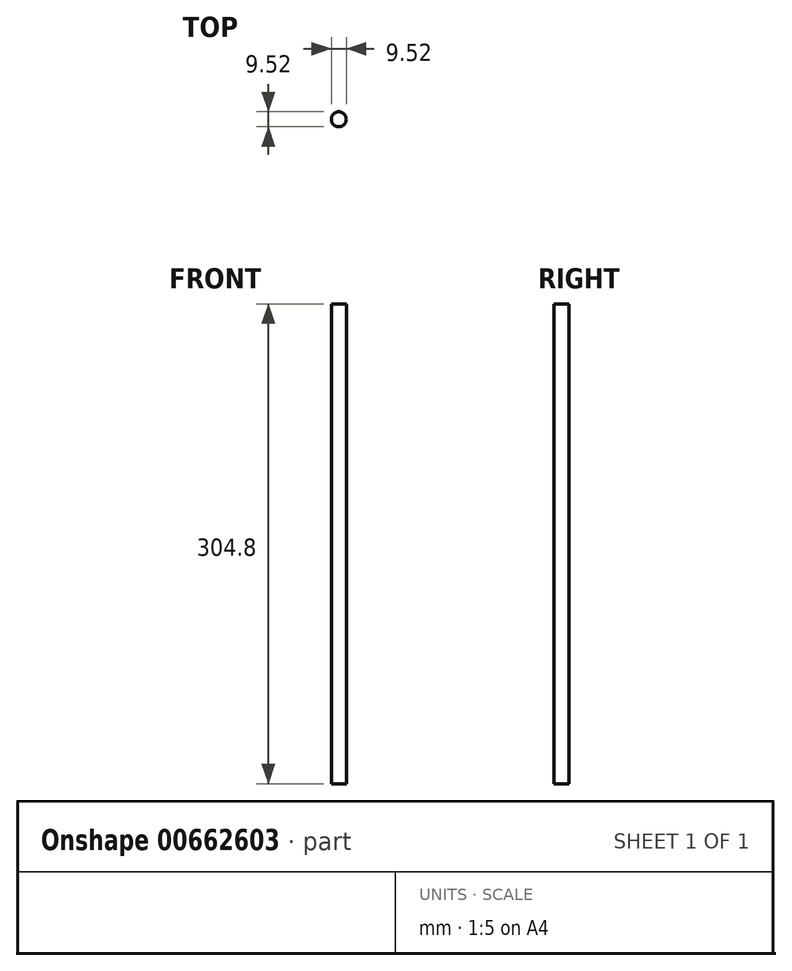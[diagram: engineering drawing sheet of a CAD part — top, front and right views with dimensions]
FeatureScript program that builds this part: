
annotation { "Feature Type Name" : "Feature", "Feature Type Description" : "" }
export const myFeature = defineFeature(function(context is Context, id is Id, definition is map)
    precondition{}
    {
        {
            var Q0;
            Q0=qCreatedBy(makeId("Top.planeOp"),FACE);
            var sketch = newSketch(context, id + "F0", { "sketchPlane" : qUnion([Q0])});
            skCircle(sketch, "E0", {"center": v(0, 0) * mm, "radius": 4.76 * mm});
            skSolve(sketch);
        }
        {
            var Q0;
            Q0=makeQuery(id+"F0.imprint","IMPRINT",FACE,{"disambiguationData":[TD([[makeQuery(id+"F0.imprint","IMPRINT",EDGE,{"derivedFrom":sQuery(id+"F0.wireOp",EDGE,"E0")}),1.0]])]});
            extrude(context, id + "F1", {"entities" : qUnion([Q0]), "depth" : 304.8 * mm, "offsetDistance" : 25.4 * mm});
        }
    });
